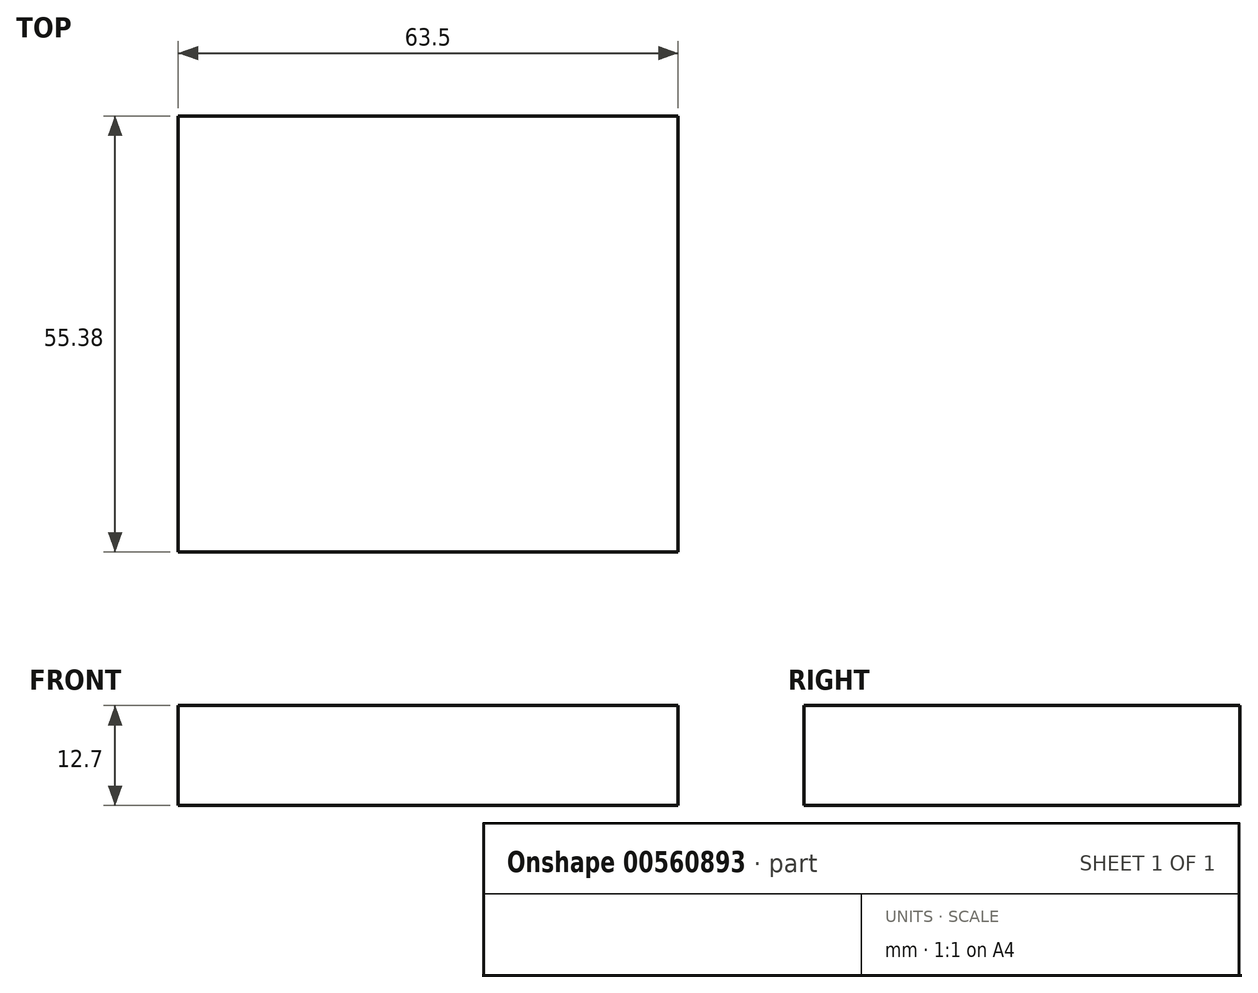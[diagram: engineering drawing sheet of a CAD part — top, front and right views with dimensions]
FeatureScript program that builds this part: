
annotation { "Feature Type Name" : "Feature", "Feature Type Description" : "" }
export const myFeature = defineFeature(function(context is Context, id is Id, definition is map)
    precondition{}
    {
        {
            var Q0;
            Q0=qCreatedBy(makeId("Top.planeOp"),FACE);
            var sketch = newSketch(context, id + "F0", { "sketchPlane" : qUnion([Q0])});
            skLineSegment(sketch, "E0.bottom", {"start": v(-31.75, 27.69) * mm, "end": v(31.75, 27.69) * mm});
            skLineSegment(sketch, "E0.top", {"start": v(-31.75, -27.69) * mm, "end": v(31.75, -27.69) * mm});
            skLineSegment(sketch, "E0.left", {"start": v(-31.75, 27.69) * mm, "end": v(-31.75, -27.69) * mm});
            skLineSegment(sketch, "E0.right", {"start": v(31.75, 27.69) * mm, "end": v(31.75, -27.69) * mm});
            skPoint(sketch, "E0.middle", {"position": v(0, 0) * mm});
            skSolve(sketch);
        }
        {
            var Q0;
            Q0 = qSketchRegion(id + "F0", true);
            extrude(context, id + "F1", {"entities" : qUnion([Q0]), "depth" : 12.7 * mm, "offsetDistance" : 25.4 * mm});
        }
    });
